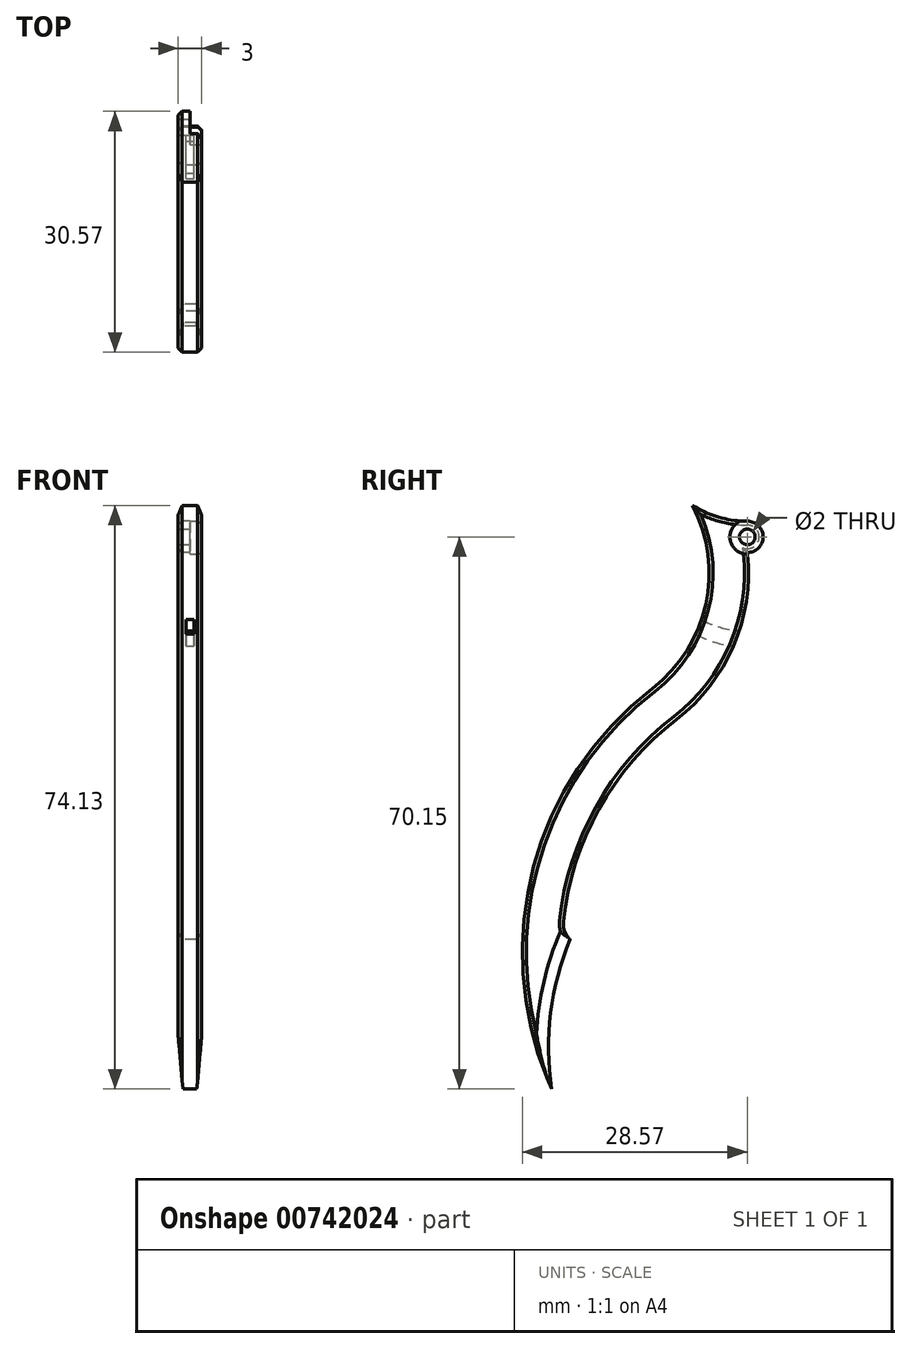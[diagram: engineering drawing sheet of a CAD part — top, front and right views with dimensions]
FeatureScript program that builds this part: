
annotation { "Feature Type Name" : "Feature", "Feature Type Description" : "" }
export const myFeature = defineFeature(function(context is Context, id is Id, definition is map)
    precondition{}
    {
        {
            var Q0;
            Q0=qCreatedBy(makeId("Right.planeOp"),FACE);
            var sketch = newSketch(context, id + "F0", { "sketchPlane" : qUnion([Q0])});
            skCircle(sketch, "E0", {"center": v(0, 0) * mm, "radius": 2 * mm});
            skArc(sketch, "E1", {"start": v(-12.06, -19.25) * mm, "mid": v(-5.28, -8.56) * mm, "end": v(-6.97, 3.98) * mm});
            skArc(sketch, "E2", {"start": v(-12.06, -19.25) * mm, "mid": v(-27.3, -42.48) * mm, "end": v(-24.85, -70.15) * mm});
            skArc(sketch, "E3", {"start": v(-9.01, -23.2) * mm, "mid": v(-18.82, -34.57) * mm, "end": v(-23.36, -48.87) * mm});
            skArc(sketch, "E4", {"start": v(-9.01, -23.2) * mm, "mid": v(-1.72, -13.79) * mm, "end": v(0, -2) * mm});
            skArc(sketch, "E5", {"start": v(-23.36, -48.87) * mm, "mid": v(-23.2, -50.11) * mm, "end": v(-22.5, -51.16) * mm});
            skArc(sketch, "E6", {"start": v(-22.5, -51.16) * mm, "mid": v(-25, -60.49) * mm, "end": v(-24.85, -70.15) * mm});
            skArc(sketch, "E7", {"start": v(-6.97, 3.98) * mm, "mid": v(-3.62, 2.5) * mm, "end": v(0, 2) * mm});
            skSolve(sketch);
        }
        {
            var Q0;
            Q0 = qSketchRegion(id + "F0", true);
            extrude(context, id + "F1", {"entities" : qUnion([Q0]), "depth" : 3 * mm, "offsetDistance" : 25 * mm});
        }
        {
            var Q0;
            Q0=makeQuery(id+"F1.opExtrude","CAP_FACE",FACE,{"disambiguationData":[OSD([sQuery(id+"F0.wireOp",EDGE,"E0"),sQuery(id+"F0.wireOp",EDGE,"E1"),sQuery(id+"F0.wireOp",EDGE,"E2"),sQuery(id+"F0.wireOp",EDGE,"E3"),sQuery(id+"F0.wireOp",EDGE,"E4"),sQuery(id+"F0.wireOp",EDGE,"E5"),sQuery(id+"F0.wireOp",EDGE,"E6"),sQuery(id+"F0.wireOp",EDGE,"E7")])],"isStart":false});
            var Q1;
            Q1=makeQuery(id+"F1.opExtrude","CAP_FACE",FACE,{"disambiguationData":[OSD([sQuery(id+"F0.wireOp",EDGE,"E0"),sQuery(id+"F0.wireOp",EDGE,"E1"),sQuery(id+"F0.wireOp",EDGE,"E2"),sQuery(id+"F0.wireOp",EDGE,"E3"),sQuery(id+"F0.wireOp",EDGE,"E4"),sQuery(id+"F0.wireOp",EDGE,"E5"),sQuery(id+"F0.wireOp",EDGE,"E6"),sQuery(id+"F0.wireOp",EDGE,"E7")])],"isStart":true});
            chamfer(context, id + "F2", {"entities" : qUnion([Q0, Q1]), "width" : 0.5 * mm, "tangentPropagation" : true});
        }
        {
            var Q0;
            Q0=makeQuery(id+"F1.opExtrude","CAP_FACE",FACE,{"disambiguationData":[OSD([sQuery(id+"F0.wireOp",EDGE,"E0"),sQuery(id+"F0.wireOp",EDGE,"E1"),sQuery(id+"F0.wireOp",EDGE,"E2"),sQuery(id+"F0.wireOp",EDGE,"E3"),sQuery(id+"F0.wireOp",EDGE,"E4"),sQuery(id+"F0.wireOp",EDGE,"E5"),sQuery(id+"F0.wireOp",EDGE,"E6"),sQuery(id+"F0.wireOp",EDGE,"E7")])],"isStart":false});
            var sketch = newSketch(context, id + "F3", { "sketchPlane" : qUnion([Q0])});
            skCircle(sketch, "E8", {"center": v(0, 0) * mm, "radius": 2.2 * mm});
            skSolve(sketch);
        }
        {
            var Q0;
            Q0 = qSketchRegion(id + "F3", true);
            extrude(context, id + "F4", {"entities" : qUnion([Q0]), "operationType" : NewBodyOperationType.REMOVE, "oppositeDirection" : true, "depth" : 1.5 * mm, "offsetDistance" : 25 * mm});
        }
        {
            var Q0;
            Q0=makeQuery(id+"F4.boolean.opBoolean","COPY",FACE,{"derivedFrom":makeQuery(id+"F4.opExtrude","CAP_FACE",FACE,{"disambiguationData":[OSD([sQuery(id+"F3.wireOp",EDGE,"E8")])],"isStart":false})});
            var sketch = newSketch(context, id + "F5", { "sketchPlane" : qUnion([Q0])});
            skCircle(sketch, "E9", {"center": v(0, 0) * mm, "radius": 1 * mm});
            skSolve(sketch);
        }
        {
            var Q0;
            Q0 = qSketchRegion(id + "F5", true);
            extrude(context, id + "F6", {"entities" : qUnion([Q0]), "operationType" : NewBodyOperationType.REMOVE, "oppositeDirection" : true, "depth" : 25 * mm, "offsetDistance" : 25 * mm});
        }
        {
            var Q0;
            {var subQ0=sQuery(id+"F0.wireOp",EDGE,"E6");Q0=makeQuery(id+"F2.opChamfer","BLEND_EDGE",EDGE,{"blendedFrom":[makeQuery(id+"F1.opExtrude","CAP_EDGE",EDGE,{"disambiguationData":[OSD([subQ0])],"isStart":true}),makeQuery(id+"F1.opExtrude","CAP_FACE",FACE,{"disambiguationData":[OSD([sQuery(id+"F0.wireOp",EDGE,"E0"),sQuery(id+"F0.wireOp",EDGE,"E1"),sQuery(id+"F0.wireOp",EDGE,"E2"),sQuery(id+"F0.wireOp",EDGE,"E3"),sQuery(id+"F0.wireOp",EDGE,"E4"),sQuery(id+"F0.wireOp",EDGE,"E5"),subQ0,sQuery(id+"F0.wireOp",EDGE,"E7")])],"isStart":true})],"blendedInto":[makeQuery(id+"F1.opExtrude","CAP_FACE",FACE,{"disambiguationData":[OSD([sQuery(id+"F0.wireOp",EDGE,"E0"),sQuery(id+"F0.wireOp",EDGE,"E1"),sQuery(id+"F0.wireOp",EDGE,"E2"),sQuery(id+"F0.wireOp",EDGE,"E3"),sQuery(id+"F0.wireOp",EDGE,"E4"),sQuery(id+"F0.wireOp",EDGE,"E5"),subQ0,sQuery(id+"F0.wireOp",EDGE,"E7")])],"isStart":true})]});}
            var Q1;
            {var subQ0=sQuery(id+"F0.wireOp",EDGE,"E6");Q1=makeQuery(id+"F2.opChamfer","BLEND_EDGE",EDGE,{"blendedFrom":[makeQuery(id+"F1.opExtrude","CAP_EDGE",EDGE,{"disambiguationData":[OSD([subQ0])],"isStart":false}),makeQuery(id+"F1.opExtrude","CAP_FACE",FACE,{"disambiguationData":[OSD([sQuery(id+"F0.wireOp",EDGE,"E0"),sQuery(id+"F0.wireOp",EDGE,"E1"),sQuery(id+"F0.wireOp",EDGE,"E2"),sQuery(id+"F0.wireOp",EDGE,"E3"),sQuery(id+"F0.wireOp",EDGE,"E4"),sQuery(id+"F0.wireOp",EDGE,"E5"),subQ0,sQuery(id+"F0.wireOp",EDGE,"E7")])],"isStart":false})],"blendedInto":[makeQuery(id+"F1.opExtrude","CAP_FACE",FACE,{"disambiguationData":[OSD([sQuery(id+"F0.wireOp",EDGE,"E0"),sQuery(id+"F0.wireOp",EDGE,"E1"),sQuery(id+"F0.wireOp",EDGE,"E2"),sQuery(id+"F0.wireOp",EDGE,"E3"),sQuery(id+"F0.wireOp",EDGE,"E4"),sQuery(id+"F0.wireOp",EDGE,"E5"),subQ0,sQuery(id+"F0.wireOp",EDGE,"E7")])],"isStart":false})]});}
            chamfer(context, id + "F7", {"entities" : qUnion([Q0, Q1]), "width" : 2.5 * mm, "tangentPropagation" : true});
        }
        {
            var Q0;
            Q0=makeQuery(id+"F1.opExtrude","CAP_FACE",FACE,{"disambiguationData":[OSD([sQuery(id+"F0.wireOp",EDGE,"E0"),sQuery(id+"F0.wireOp",EDGE,"E1"),sQuery(id+"F0.wireOp",EDGE,"E2"),sQuery(id+"F0.wireOp",EDGE,"E3"),sQuery(id+"F0.wireOp",EDGE,"E4"),sQuery(id+"F0.wireOp",EDGE,"E5"),sQuery(id+"F0.wireOp",EDGE,"E6"),sQuery(id+"F0.wireOp",EDGE,"E7")])],"isStart":false});
            var sketch = newSketch(context, id + "F8", { "sketchPlane" : qUnion([Q0])});
            skCircle(sketch, "E10", {"center": v(0, 0) * mm, "radius": 13 * mm, "construction": true});
            skCircle(sketch, "E11", {"center": v(0, 0) * mm, "radius": 12 * mm});
            skCircle(sketch, "E12", {"center": v(0, 0) * mm, "radius": 14 * mm});
            skLineSegment(sketch, "E13", {"start": v(-12, 0) * mm, "end": v(-14, 0) * mm});
            skPoint(sketch, "E14", {"position": v(-13, 0) * mm});
            skSolve(sketch);
        }
        {
            var Q0;
            Q0 = qSketchRegion(id + "F8", true);
            extrude(context, id + "F9", {"entities" : qUnion([Q0]), "operationType" : NewBodyOperationType.REMOVE, "oppositeDirection" : true, "depth" : 2 * mm, "offsetDistance" : 25 * mm, "hasSecondDirection" : true, "secondDirectionOppositeDirection" : true, "secondDirectionDepth" : 1 * mm});
        }
    });
